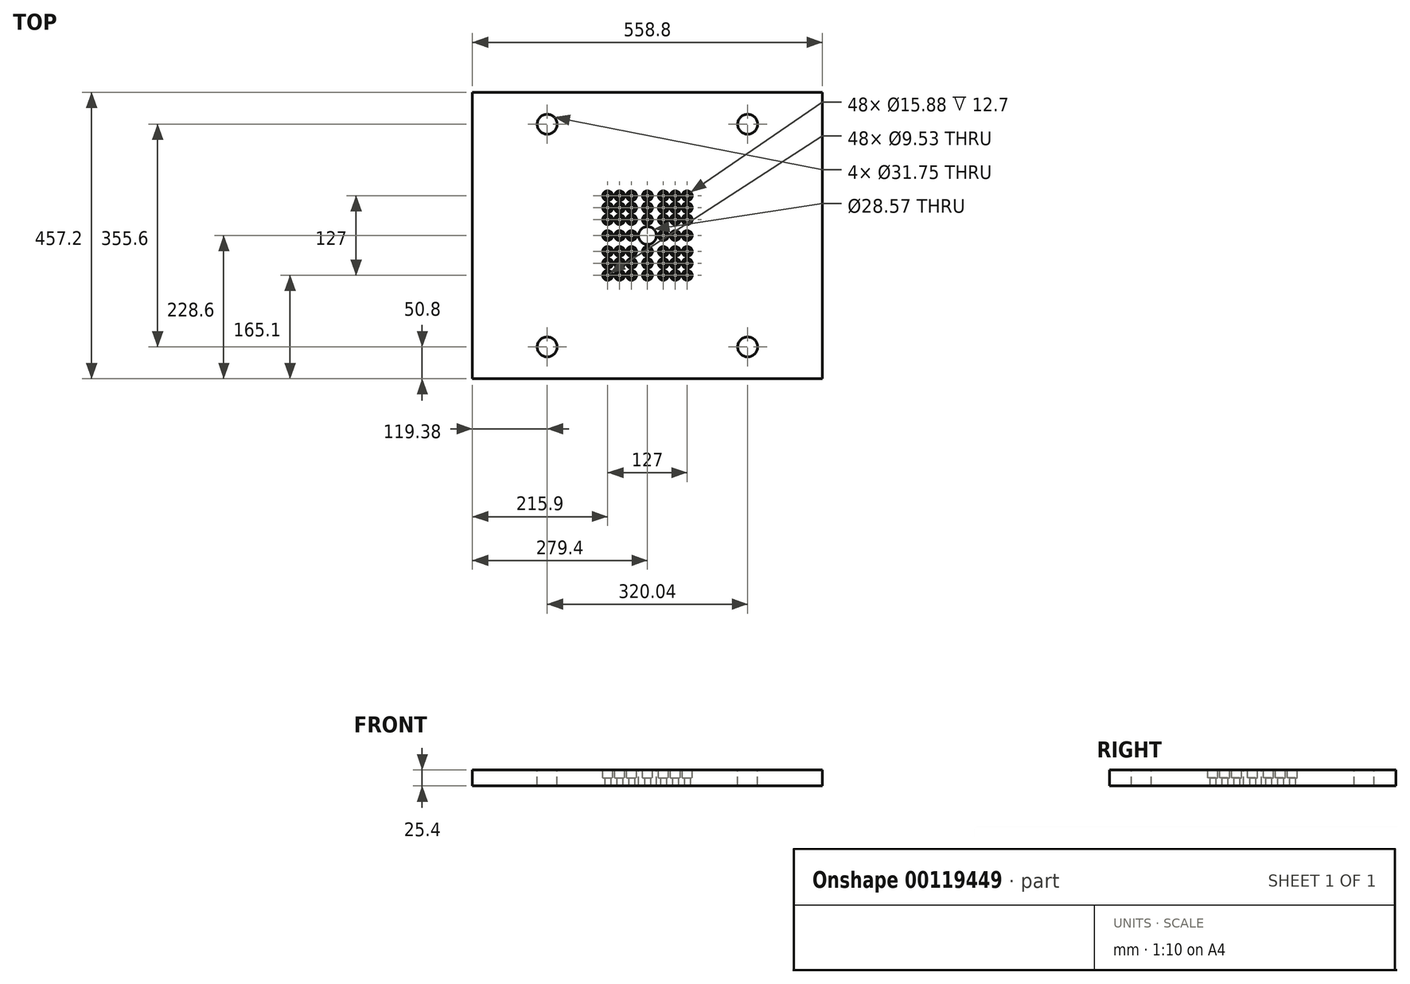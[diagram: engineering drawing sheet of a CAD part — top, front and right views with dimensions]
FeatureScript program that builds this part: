
annotation { "Feature Type Name" : "Feature", "Feature Type Description" : "" }
export const myFeature = defineFeature(function(context is Context, id is Id, definition is map)
    precondition{}
    {
        {
            var Q0;
            Q0=qCreatedBy(makeId("Top.planeOp"),FACE);
            var sketch = newSketch(context, id + "F0", { "sketchPlane" : qUnion([Q0])});
            skLineSegment(sketch, "E0.bottom", {"start": v(279.4, -228.6) * mm, "end": v(-279.4, -228.6) * mm});
            skLineSegment(sketch, "E0.top", {"start": v(279.4, 228.6) * mm, "end": v(-279.4, 228.6) * mm});
            skLineSegment(sketch, "E0.left", {"start": v(279.4, -228.6) * mm, "end": v(279.4, 228.6) * mm});
            skLineSegment(sketch, "E0.right", {"start": v(-279.4, -228.6) * mm, "end": v(-279.4, 228.6) * mm});
            skPoint(sketch, "E0.middle", {"position": v(0, 0) * mm});
            skSolve(sketch);
        }
        {
            var Q0;
            Q0 = qSketchRegion(id + "F0", true);
            extrude(context, id + "F1", {"entities" : qUnion([Q0]), "oppositeDirection" : true, "depth" : 25.4 * mm});
        }
        {
            var Q0;
            Q0=makeQuery(id+"F1.opExtrude","CAP_FACE",FACE,{"disambiguationData":[OSD([sQuery(id+"F0.wireOp",EDGE,"E0.bottom"),sQuery(id+"F0.wireOp",EDGE,"E0.top"),sQuery(id+"F0.wireOp",EDGE,"E0.left"),sQuery(id+"F0.wireOp",EDGE,"E0.right")])],"isStart":true});
            var sketch = newSketch(context, id + "F2", { "sketchPlane" : qUnion([Q0])});
            skCircle(sketch, "E1", {"center": v(-160.02, -177.8) * mm, "radius": 15.88 * mm});
            skCircle(sketch, "E2", {"center": v(160.02, -177.8) * mm, "radius": 15.88 * mm});
            skCircle(sketch, "E3", {"center": v(-160.02, 177.8) * mm, "radius": 15.88 * mm});
            skCircle(sketch, "E4", {"center": v(160.02, 177.8) * mm, "radius": 15.88 * mm});
            skLineSegment(sketch, "E5", {"start": v(-160.02, 177.8) * mm, "end": v(-279.4, 177.8) * mm});
            skLineSegment(sketch, "E6", {"start": v(160.02, 177.8) * mm, "end": v(279.4, 177.8) * mm});
            skSolve(sketch);
        }
        {
            var Q0;
            Q0 = qSketchRegion(id + "F2", true);
            extrude(context, id + "F3", {"entities" : qUnion([Q0]), "operationType" : NewBodyOperationType.REMOVE, "endBound" : BoundingType.THROUGH_ALL, "oppositeDirection" : true, "depth" : 25.4 * mm});
        }
        {
            var Q0;
            Q0=makeQuery(id+"F1.opExtrude","CAP_FACE",FACE,{"disambiguationData":[OSD([sQuery(id+"F0.wireOp",EDGE,"E0.bottom"),sQuery(id+"F0.wireOp",EDGE,"E0.top"),sQuery(id+"F0.wireOp",EDGE,"E0.left"),sQuery(id+"F0.wireOp",EDGE,"E0.right")])],"isStart":true});
            var sketch = newSketch(context, id + "F4", { "sketchPlane" : qUnion([Q0])});
            skCircle(sketch, "E7", {"center": v(0, 0) * mm, "radius": 14.29 * mm});
            skCircle(sketch, "E8", {"center": v(-63.5, 63.5) * mm, "radius": 7.94 * mm});
            skCircle(sketch, "E9", {"center": v(-44.45, 63.5) * mm, "radius": 7.94 * mm});
            skCircle(sketch, "E10", {"center": v(-25.4, 63.5) * mm, "radius": 7.94 * mm});
            skCircle(sketch, "E11", {"center": v(-63.5, 44.45) * mm, "radius": 7.94 * mm});
            skCircle(sketch, "E12", {"center": v(-63.5, 25.4) * mm, "radius": 7.94 * mm});
            skCircle(sketch, "E13", {"center": v(-44.45, 44.45) * mm, "radius": 7.94 * mm});
            skCircle(sketch, "E14", {"center": v(-25.4, 44.45) * mm, "radius": 7.94 * mm});
            skCircle(sketch, "E15", {"center": v(-44.45, 25.4) * mm, "radius": 7.94 * mm});
            skCircle(sketch, "E16", {"center": v(-25.4, 25.4) * mm, "radius": 7.94 * mm});
            skCircle(sketch, "E17", {"center": v(0, 63.5) * mm, "radius": 7.94 * mm});
            skCircle(sketch, "E18", {"center": v(0, 44.45) * mm, "radius": 7.94 * mm});
            skCircle(sketch, "E19", {"center": v(0, 25.4) * mm, "radius": 7.94 * mm});
            skCircle(sketch, "E20", {"center": v(25.4, 63.5) * mm, "radius": 7.94 * mm});
            skCircle(sketch, "E21", {"center": v(44.45, 63.5) * mm, "radius": 7.94 * mm});
            skCircle(sketch, "E22", {"center": v(63.5, 63.5) * mm, "radius": 7.94 * mm});
            skCircle(sketch, "E23", {"center": v(25.4, 44.45) * mm, "radius": 7.94 * mm});
            skCircle(sketch, "E24", {"center": v(25.4, 25.4) * mm, "radius": 7.94 * mm});
            skCircle(sketch, "E25", {"center": v(44.45, 44.45) * mm, "radius": 7.94 * mm});
            skCircle(sketch, "E26", {"center": v(63.5, 44.45) * mm, "radius": 7.94 * mm});
            skCircle(sketch, "E27", {"center": v(44.45, 25.4) * mm, "radius": 7.94 * mm});
            skCircle(sketch, "E28", {"center": v(63.5, 25.4) * mm, "radius": 7.94 * mm});
            skCircle(sketch, "E29", {"center": v(-63.5, 0) * mm, "radius": 7.94 * mm});
            skCircle(sketch, "E30", {"center": v(-44.45, 0) * mm, "radius": 7.94 * mm});
            skCircle(sketch, "E31", {"center": v(-25.4, 0) * mm, "radius": 7.94 * mm});
            skCircle(sketch, "E32", {"center": v(-63.5, -25.4) * mm, "radius": 7.94 * mm});
            skCircle(sketch, "E33", {"center": v(-63.5, -44.45) * mm, "radius": 7.94 * mm});
            skCircle(sketch, "E34", {"center": v(-44.45, -25.4) * mm, "radius": 7.94 * mm});
            skCircle(sketch, "E35", {"center": v(-25.4, -25.4) * mm, "radius": 7.94 * mm});
            skCircle(sketch, "E36", {"center": v(-44.45, -44.45) * mm, "radius": 7.94 * mm});
            skCircle(sketch, "E37", {"center": v(-25.4, -44.45) * mm, "radius": 7.94 * mm});
            skCircle(sketch, "E38", {"center": v(-63.5, -63.5) * mm, "radius": 7.94 * mm});
            skCircle(sketch, "E39", {"center": v(-44.45, -63.5) * mm, "radius": 7.94 * mm});
            skCircle(sketch, "E40", {"center": v(-25.4, -63.5) * mm, "radius": 7.94 * mm});
            skCircle(sketch, "E41", {"center": v(0, -25.4) * mm, "radius": 7.94 * mm});
            skCircle(sketch, "E42", {"center": v(0, -44.45) * mm, "radius": 7.94 * mm});
            skCircle(sketch, "E43", {"center": v(0, -63.5) * mm, "radius": 7.94 * mm});
            skCircle(sketch, "E44", {"center": v(25.4, 0) * mm, "radius": 7.94 * mm});
            skCircle(sketch, "E45", {"center": v(44.45, 0) * mm, "radius": 7.94 * mm});
            skCircle(sketch, "E46", {"center": v(63.5, 0) * mm, "radius": 7.94 * mm});
            skCircle(sketch, "E47", {"center": v(25.4, -25.4) * mm, "radius": 7.94 * mm});
            skCircle(sketch, "E48", {"center": v(44.45, -25.4) * mm, "radius": 7.94 * mm});
            skCircle(sketch, "E49", {"center": v(63.5, -25.4) * mm, "radius": 7.94 * mm});
            skCircle(sketch, "E50", {"center": v(25.4, -44.45) * mm, "radius": 7.94 * mm});
            skCircle(sketch, "E51", {"center": v(44.45, -44.45) * mm, "radius": 7.94 * mm});
            skCircle(sketch, "E52", {"center": v(63.5, -44.45) * mm, "radius": 7.94 * mm});
            skCircle(sketch, "E53", {"center": v(25.4, -63.5) * mm, "radius": 7.94 * mm});
            skCircle(sketch, "E54", {"center": v(44.45, -63.5) * mm, "radius": 7.94 * mm});
            skCircle(sketch, "E55", {"center": v(63.5, -63.5) * mm, "radius": 7.94 * mm});
            skLineSegment(sketch, "E56", {"start": v(-71.44, -25.4) * mm, "end": v(-279.4, -25.4) * mm});
            skLineSegment(sketch, "E57", {"start": v(71.44, -25.4) * mm, "end": v(279.4, -25.4) * mm});
            skLineSegment(sketch, "E58", {"start": v(0, 63.5) * mm, "end": v(0, 228.6) * mm});
            skLineSegment(sketch, "E59", {"start": v(0, -63.5) * mm, "end": v(0, -228.6) * mm});
            skSolve(sketch);
        }
        {
            var Q0;
            Q0 = qSketchRegion(id + "F4", true);
            extrude(context, id + "F5", {"entities" : qUnion([Q0]), "operationType" : NewBodyOperationType.REMOVE, "endBound" : BoundingType.THROUGH_ALL, "oppositeDirection" : true, "depth" : 25.4 * mm});
        }
        {
            var Q0;
            Q0=makeQuery(id+"F1.opExtrude","CAP_FACE",FACE,{"disambiguationData":[OSD([sQuery(id+"F0.wireOp",EDGE,"E0.bottom"),sQuery(id+"F0.wireOp",EDGE,"E0.top"),sQuery(id+"F0.wireOp",EDGE,"E0.left"),sQuery(id+"F0.wireOp",EDGE,"E0.right")])],"isStart":false});
            var sketch = newSketch(context, id + "F6", { "sketchPlane" : qUnion([Q0])});
            skCircle(sketch, "E60.0", {"center": v(63.5, 63.5) * mm, "radius": 7.94 * mm});
            skCircle(sketch, "E60.1", {"center": v(63.5, 44.45) * mm, "radius": 7.94 * mm});
            skCircle(sketch, "E60.2", {"center": v(44.45, 44.45) * mm, "radius": 7.94 * mm});
            skCircle(sketch, "E60.3", {"center": v(44.45, 63.5) * mm, "radius": 7.94 * mm});
            skCircle(sketch, "E60.4", {"center": v(25.4, 63.5) * mm, "radius": 7.94 * mm});
            skCircle(sketch, "E60.5", {"center": v(25.4, 44.45) * mm, "radius": 7.94 * mm});
            skCircle(sketch, "E60.6", {"center": v(25.4, 25.4) * mm, "radius": 7.94 * mm});
            skCircle(sketch, "E60.7", {"center": v(44.45, 25.4) * mm, "radius": 7.94 * mm});
            skCircle(sketch, "E60.8", {"center": v(63.5, 25.4) * mm, "radius": 7.94 * mm});
            skCircle(sketch, "E60.9", {"center": v(63.5, 0) * mm, "radius": 7.94 * mm});
            skCircle(sketch, "E60.10", {"center": v(44.45, 0) * mm, "radius": 7.94 * mm});
            skCircle(sketch, "E60.11", {"center": v(25.4, 0) * mm, "radius": 7.94 * mm});
            skCircle(sketch, "E60.12", {"center": v(25.4, -25.4) * mm, "radius": 7.94 * mm});
            skCircle(sketch, "E60.13", {"center": v(44.45, -25.4) * mm, "radius": 7.94 * mm});
            skCircle(sketch, "E60.14", {"center": v(63.5, -25.4) * mm, "radius": 7.94 * mm});
            skCircle(sketch, "E60.15", {"center": v(63.5, -44.45) * mm, "radius": 7.94 * mm});
            skCircle(sketch, "E60.16", {"center": v(44.45, -44.45) * mm, "radius": 7.94 * mm});
            skCircle(sketch, "E60.17", {"center": v(25.4, -44.45) * mm, "radius": 7.94 * mm});
            skCircle(sketch, "E60.18", {"center": v(25.4, -63.5) * mm, "radius": 7.94 * mm});
            skCircle(sketch, "E60.19", {"center": v(44.45, -63.5) * mm, "radius": 7.94 * mm});
            skCircle(sketch, "E60.20", {"center": v(63.5, -63.5) * mm, "radius": 7.94 * mm});
            skCircle(sketch, "E60.21", {"center": v(0, -25.4) * mm, "radius": 7.94 * mm});
            skCircle(sketch, "E60.22", {"center": v(0, -44.45) * mm, "radius": 7.94 * mm});
            skCircle(sketch, "E60.23", {"center": v(0, -63.5) * mm, "radius": 7.94 * mm});
            skCircle(sketch, "E61.0", {"center": v(0, 63.5) * mm, "radius": 7.94 * mm});
            skCircle(sketch, "E61.1", {"center": v(0, 44.45) * mm, "radius": 7.94 * mm});
            skCircle(sketch, "E61.2", {"center": v(0, 25.4) * mm, "radius": 7.94 * mm});
            skCircle(sketch, "E61.3", {"center": v(-25.4, 25.4) * mm, "radius": 7.94 * mm});
            skCircle(sketch, "E61.4", {"center": v(-25.4, 44.45) * mm, "radius": 7.94 * mm});
            skCircle(sketch, "E61.5", {"center": v(-25.4, 63.5) * mm, "radius": 7.94 * mm});
            skCircle(sketch, "E61.6", {"center": v(-44.45, 63.5) * mm, "radius": 7.94 * mm});
            skCircle(sketch, "E61.7", {"center": v(-44.45, 44.45) * mm, "radius": 7.94 * mm});
            skCircle(sketch, "E61.8", {"center": v(-44.45, 25.4) * mm, "radius": 7.94 * mm});
            skCircle(sketch, "E61.9", {"center": v(-63.5, 25.4) * mm, "radius": 7.94 * mm});
            skCircle(sketch, "E61.10", {"center": v(-63.5, 44.45) * mm, "radius": 7.94 * mm});
            skCircle(sketch, "E61.11", {"center": v(-63.5, 63.5) * mm, "radius": 7.94 * mm});
            skCircle(sketch, "E61.12", {"center": v(-63.5, 0) * mm, "radius": 7.94 * mm});
            skCircle(sketch, "E61.13", {"center": v(-44.45, 0) * mm, "radius": 7.94 * mm});
            skCircle(sketch, "E61.14", {"center": v(-25.4, 0) * mm, "radius": 7.94 * mm});
            skCircle(sketch, "E61.15", {"center": v(-25.4, -25.4) * mm, "radius": 7.94 * mm});
            skCircle(sketch, "E61.16", {"center": v(-44.45, -25.4) * mm, "radius": 7.94 * mm});
            skCircle(sketch, "E61.17", {"center": v(-63.5, -25.4) * mm, "radius": 7.94 * mm});
            skCircle(sketch, "E61.18", {"center": v(-63.5, -44.45) * mm, "radius": 7.94 * mm});
            skCircle(sketch, "E61.19", {"center": v(-44.45, -44.45) * mm, "radius": 7.94 * mm});
            skCircle(sketch, "E61.20", {"center": v(-25.4, -44.45) * mm, "radius": 7.94 * mm});
            skCircle(sketch, "E61.21", {"center": v(-25.4, -63.5) * mm, "radius": 7.94 * mm});
            skCircle(sketch, "E61.22", {"center": v(-44.45, -63.5) * mm, "radius": 7.94 * mm});
            skCircle(sketch, "E61.23", {"center": v(-63.5, -63.5) * mm, "radius": 7.94 * mm});
            skCircle(sketch, "E62", {"center": v(63.5, 63.5) * mm, "radius": 4.76 * mm});
            skCircle(sketch, "E63", {"center": v(63.5, 44.45) * mm, "radius": 4.76 * mm});
            skCircle(sketch, "E64", {"center": v(63.5, 25.4) * mm, "radius": 4.76 * mm});
            skCircle(sketch, "E65", {"center": v(44.45, 63.5) * mm, "radius": 4.76 * mm});
            skCircle(sketch, "E66", {"center": v(44.45, 44.45) * mm, "radius": 4.76 * mm});
            skCircle(sketch, "E67", {"center": v(44.45, 25.4) * mm, "radius": 4.76 * mm});
            skCircle(sketch, "E68", {"center": v(25.4, 25.4) * mm, "radius": 4.76 * mm});
            skCircle(sketch, "E69", {"center": v(25.4, 44.45) * mm, "radius": 4.76 * mm});
            skCircle(sketch, "E70", {"center": v(25.4, 63.5) * mm, "radius": 4.76 * mm});
            skCircle(sketch, "E71", {"center": v(0, 63.5) * mm, "radius": 4.76 * mm});
            skCircle(sketch, "E72", {"center": v(0, 44.45) * mm, "radius": 4.76 * mm});
            skCircle(sketch, "E73", {"center": v(0, 25.4) * mm, "radius": 4.76 * mm});
            skCircle(sketch, "E74", {"center": v(25.4, 0) * mm, "radius": 4.76 * mm});
            skCircle(sketch, "E75", {"center": v(44.45, 0) * mm, "radius": 4.76 * mm});
            skCircle(sketch, "E76", {"center": v(63.5, 0) * mm, "radius": 4.76 * mm});
            skCircle(sketch, "E77", {"center": v(-25.4, 0) * mm, "radius": 4.76 * mm});
            skCircle(sketch, "E78", {"center": v(-63.5, 0) * mm, "radius": 4.76 * mm});
            skCircle(sketch, "E79", {"center": v(-44.45, 0) * mm, "radius": 4.76 * mm});
            skCircle(sketch, "E80", {"center": v(0, -25.4) * mm, "radius": 4.76 * mm});
            skCircle(sketch, "E81", {"center": v(0, -44.45) * mm, "radius": 4.76 * mm});
            skCircle(sketch, "E82", {"center": v(0, -63.5) * mm, "radius": 4.76 * mm});
            skCircle(sketch, "E83", {"center": v(-25.4, 63.5) * mm, "radius": 4.76 * mm});
            skCircle(sketch, "E84", {"center": v(-44.45, 63.5) * mm, "radius": 4.76 * mm});
            skCircle(sketch, "E85", {"center": v(-63.5, 63.5) * mm, "radius": 4.76 * mm});
            skCircle(sketch, "E86", {"center": v(-63.5, 44.45) * mm, "radius": 4.76 * mm});
            skCircle(sketch, "E87", {"center": v(-44.45, 44.45) * mm, "radius": 4.76 * mm});
            skCircle(sketch, "E88", {"center": v(-25.4, 44.45) * mm, "radius": 4.76 * mm});
            skCircle(sketch, "E89", {"center": v(-25.4, 25.4) * mm, "radius": 4.76 * mm});
            skCircle(sketch, "E90", {"center": v(-44.45, 25.4) * mm, "radius": 4.76 * mm});
            skCircle(sketch, "E91", {"center": v(-63.5, 25.4) * mm, "radius": 4.76 * mm});
            skLineSegment(sketch, "E92", {"start": v(0, 14.29) * mm, "end": v(0, -14.29) * mm});
            skLineSegment(sketch, "E93", {"start": v(-14.29, 0) * mm, "end": v(14.29, 0) * mm});
            skCircle(sketch, "E94.MirrorC", {"center": v(-25.4, -63.5) * mm, "radius": 4.76 * mm});
            skCircle(sketch, "E95.MirrorC", {"center": v(-44.45, -63.5) * mm, "radius": 4.76 * mm});
            skCircle(sketch, "E96.MirrorC", {"center": v(-63.5, -63.5) * mm, "radius": 4.76 * mm});
            skCircle(sketch, "E97.MirrorC", {"center": v(-63.5, -44.45) * mm, "radius": 4.76 * mm});
            skCircle(sketch, "E98.MirrorC", {"center": v(-63.5, -25.4) * mm, "radius": 4.76 * mm});
            skCircle(sketch, "E99.MirrorC", {"center": v(-44.45, -25.4) * mm, "radius": 4.76 * mm});
            skCircle(sketch, "E100.MirrorC", {"center": v(-44.45, -44.45) * mm, "radius": 4.76 * mm});
            skCircle(sketch, "E101.MirrorC", {"center": v(-25.4, -44.45) * mm, "radius": 4.76 * mm});
            skCircle(sketch, "E102.MirrorC", {"center": v(-25.4, -25.4) * mm, "radius": 4.76 * mm});
            skCircle(sketch, "E103.MirrorC", {"center": v(25.4, -25.4) * mm, "radius": 4.76 * mm});
            skCircle(sketch, "E104.MirrorC", {"center": v(25.4, -44.45) * mm, "radius": 4.76 * mm});
            skCircle(sketch, "E105.MirrorC", {"center": v(25.4, -63.5) * mm, "radius": 4.76 * mm});
            skCircle(sketch, "E106.MirrorC", {"center": v(44.45, -25.4) * mm, "radius": 4.76 * mm});
            skCircle(sketch, "E107.MirrorC", {"center": v(44.45, -44.45) * mm, "radius": 4.76 * mm});
            skCircle(sketch, "E108.MirrorC", {"center": v(44.45, -63.5) * mm, "radius": 4.76 * mm});
            skCircle(sketch, "E109.MirrorC", {"center": v(63.5, -63.5) * mm, "radius": 4.76 * mm});
            skCircle(sketch, "E110.MirrorC", {"center": v(63.5, -44.45) * mm, "radius": 4.76 * mm});
            skCircle(sketch, "E111.MirrorC", {"center": v(63.5, -25.4) * mm, "radius": 4.76 * mm});
            skSolve(sketch);
        }
        {
            var Q0;
            Q0 = qSketchRegion(id + "F6", true);
            extrude(context, id + "F7", {"entities" : qUnion([Q0]), "operationType" : NewBodyOperationType.ADD, "oppositeDirection" : true, "depth" : 12.7 * mm});
        }
    });
